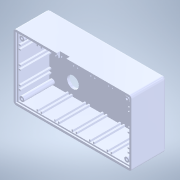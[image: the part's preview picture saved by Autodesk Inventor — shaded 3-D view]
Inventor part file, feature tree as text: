
AUTODESK INVENTOR PART (.ipt)
format: ipt  version: 2022 (Build 260153000, 153)  size: 232,960 bytes
history: native  units: mm
features: other x2, extrude x2, sketch x2
ambient origin geometry x8: Origin, YZ Plane, XZ Plane, XY Plane, X Axis, Y Axis, Z Axis, Center Point
bodies: Body1 (feature_tree)
feature tree (6):
  other  "Твердое тело1"
  extrude  "Выдавливание1"  Depth=11.0mm
  extrude  "Выдавливание2"  Depth=10.0mm TaperAngle=0.0deg
  sketch  "Эскиз1"
  sketch  "Эскиз2"
  other  "Ñêðóãëåíèå1"
